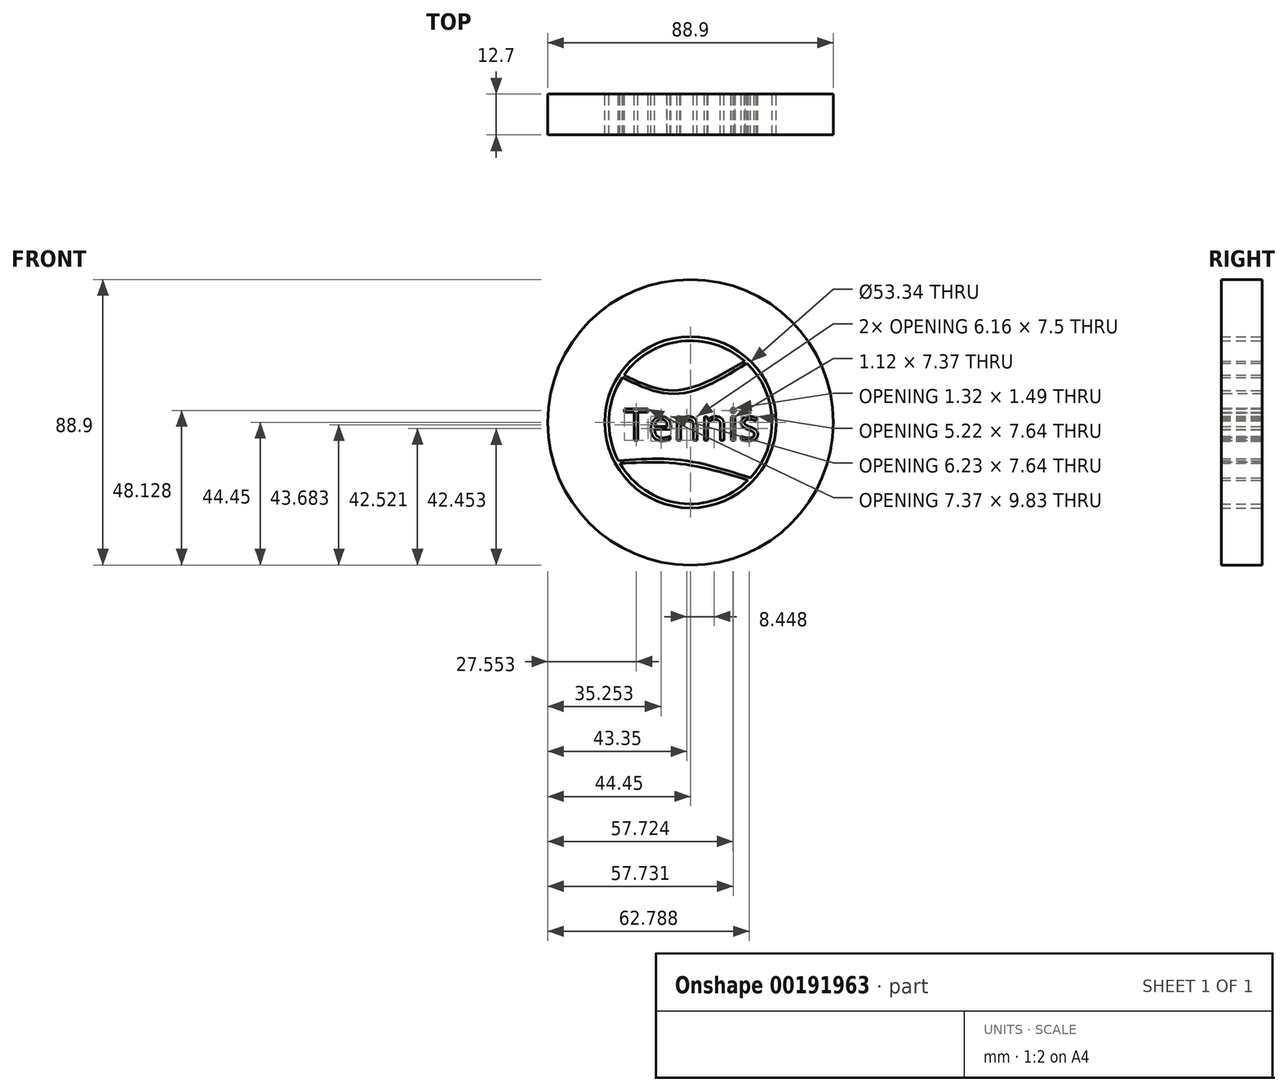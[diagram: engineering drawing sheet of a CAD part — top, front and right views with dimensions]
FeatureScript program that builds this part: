
annotation { "Feature Type Name" : "Feature", "Feature Type Description" : "" }
export const myFeature = defineFeature(function(context is Context, id is Id, definition is map)
    precondition{}
    {
        {
            var Q0;
            Q0=qCreatedBy(makeId("Front.planeOp"),FACE);
            var sketch = newSketch(context, id + "F0", { "sketchPlane" : qUnion([Q0])});
            skCircle(sketch, "E0", {"center": v(0, 0) * mm, "radius": 44.45 * mm});
            skCircle(sketch, "E1", {"center": v(0, 0) * mm, "radius": 25.4 * mm});
            skFitSpline(sketch, "E2", {"points": [v(-21.24, 13.93) * mm, v(-4.08, 8.9) * mm, v(17.58, 18.34) * mm], "startDerivative": vector(36, -17.42) * mm, "endDerivative": vector(41.44, 25.25) * mm});
            skFitSpline(sketch, "E3", {"points": [v(-22.41, -11.95) * mm, v(-2.62, -11.8) * mm, v(18.61, -17.28) * mm], "startDerivative": vector(40.39, 2.94) * mm, "endDerivative": vector(41.58, -13.45) * mm});
            skText(sketch, "E4", { "text": "Tennis\n", "fontName": "OpenSans-Regular.ttf"});
            skCircle(sketch, "E5", {"center": v(0, 0) * mm, "radius": 26.67 * mm});
            skFitSpline(sketch, "E6", {"points": [v(-20.72, 14.69) * mm, v(-4.32, 9.96) * mm, v(16.84, 19.02) * mm], "startDerivative": vector(34.52, -16.47) * mm, "endDerivative": vector(40.41, 24.1) * mm});
            skFitSpline(sketch, "E7", {"points": [v(-21.95, -12.77) * mm, v(-2.77, -12.98) * mm, v(17.9, -18.01) * mm], "startDerivative": vector(39.16, 1.87) * mm, "endDerivative": vector(40.53, -12.23) * mm});
            const initialGuessF0  = {"E4": [-0.0207, -0.00568, 1, 0, 0.00991]};
            skSetInitialGuess(sketch, initialGuessF0);
            skSolve(sketch);
        }
        {
            var Q0;
            Q0=makeQuery(id+"F0.imprint","IMPRINT",FACE,{"disambiguationData":[TD([[makeQuery(id+"F0.imprint","IMPRINT",EDGE,{"derivedFrom":sQuery(id+"F0.wireOp",EDGE,"E0")}),1.0]])]});
            var Q1;
            {var subQ0=sQuery(id+"F0.wireOp",EDGE,"E6");Q1=makeQuery(id+"F0.imprint","IMPRINT",FACE,{"disambiguationData":[TD([[makeQuery(id+"F0.imprint","IMPRINT",EDGE,{"derivedFrom":subQ0}),1.0]])]});}
            var Q2;
            {var subQ0=sQuery(id+"F0.wireOp",EDGE,"E2");Q2=makeQuery(id+"F0.imprint","IMPRINT",FACE,{"disambiguationData":[TD([[makeQuery(id+"F0.imprint","IMPRINT",EDGE,{"derivedFrom":subQ0}),-1.0]])]});}
            var Q3;
            {var subQ0=sQuery(id+"F0.wireOp",EDGE,"E7");Q3=makeQuery(id+"F0.imprint","IMPRINT",FACE,{"disambiguationData":[TD([[makeQuery(id+"F0.imprint","IMPRINT",EDGE,{"derivedFrom":subQ0}),-1.0]])]});}
            var Q4;
            Q4=makeQuery(id+"F0.imprint","IMPRINT",FACE,{"disambiguationData":[TD([[makeQuery(id+"F0.imprint","IMPRINT",EDGE,{"derivedFrom":sQuery(id+"F0.wireOp",EDGE,"E4.sketch_text.stroke-22")}),1.0]])]});
            extrude(context, id + "F1", {"entities" : qUnion([Q0, Q1, Q2, Q3, Q4]), "depth" : 12.7 * mm});
        }
    });
